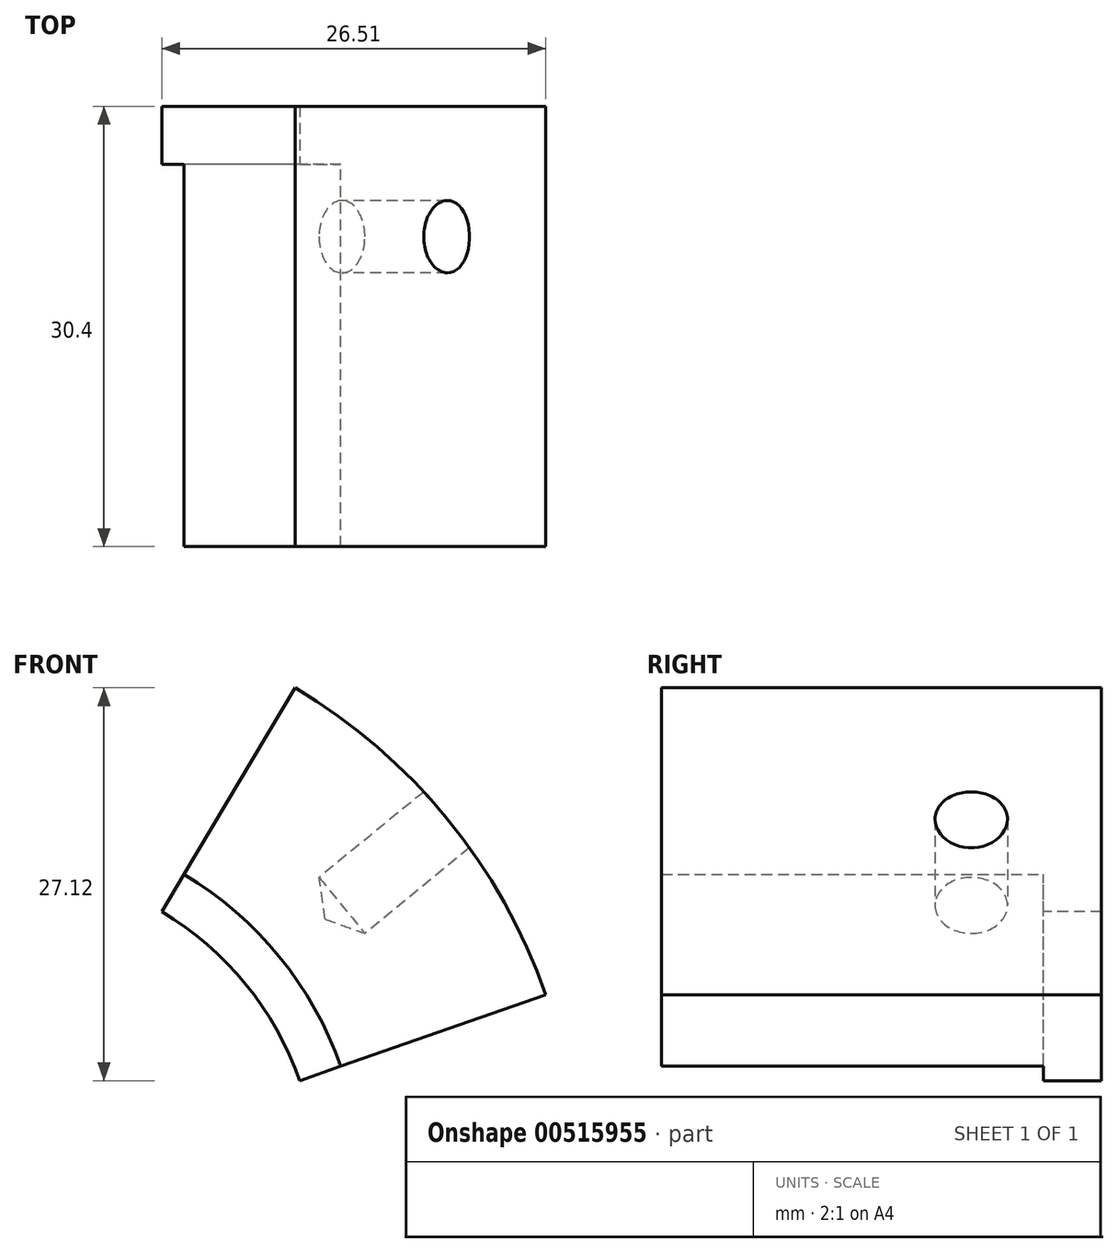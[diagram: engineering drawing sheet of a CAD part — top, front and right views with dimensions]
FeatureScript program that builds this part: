
annotation { "Feature Type Name" : "Feature", "Feature Type Description" : "" }
export const myFeature = defineFeature(function(context is Context, id is Id, definition is map)
    precondition{}
    {
        {
            var Q0;
            Q0=qCreatedBy(makeId("Front.planeOp"),FACE);
            var sketch = newSketch(context, id + "F0", { "sketchPlane" : qUnion([Q0])});
            skArc(sketch, "E0", {"start": v(37.76, 13.18) * mm, "mid": v(30.98, 25.3) * mm, "end": v(20.45, 34.37) * mm});
            skArc(sketch, "E1", {"start": v(23.6, 8.24) * mm, "mid": v(19.36, 15.82) * mm, "end": v(12.78, 21.48) * mm});
            skLineSegment(sketch, "E2", {"start": v(12.78, 21.48) * mm, "end": v(20.45, 34.37) * mm});
            skLineSegment(sketch, "E3", {"start": v(23.6, 8.24) * mm, "end": v(37.76, 13.18) * mm});
            skSolve(sketch);
        }
        {
            var Q0;
            Q0=qCreatedBy(makeId("Front.planeOp"),FACE);
            var sketch = newSketch(context, id + "F1", { "sketchPlane" : qUnion([Q0])});
            skArc(sketch, "E4", {"start": v(20.77, 7.25) * mm, "mid": v(17.04, 13.92) * mm, "end": v(11.25, 18.9) * mm});
            skLineSegment(sketch, "E5", {"start": v(20.5, 34.46) * mm, "end": v(11.25, 18.9) * mm});
            skLineSegment(sketch, "E6", {"start": v(37.76, 13.18) * mm, "end": v(20.77, 7.25) * mm});
            skArc(sketch, "E7", {"start": v(37.76, 13.18) * mm, "mid": v(30.98, 25.3) * mm, "end": v(20.45, 34.37) * mm});
            skSolve(sketch);
        }
        {
            var Q0;
            Q0=makeQuery(id+"F0.imprint","IMPRINT",FACE,{"disambiguationData":[TD([[makeQuery(id+"F0.imprint","IMPRINT",EDGE,{"derivedFrom":sQuery(id+"F0.wireOp",EDGE,"E0")}),1.0]])]});
            extrude(context, id + "F2", {"entities" : qUnion([Q0]), "depth" : 26.4 * mm, "offsetDistance" : 25 * mm});
        }
        {
            var Q0;
            Q0 = qSketchRegion(id + "F1", true);
            var Q1;
            Q1 = qSketchRegion(id + "F0", true);
            extrude(context, id + "F3", {"entities" : qUnion([Q0, Q1]), "operationType" : NewBodyOperationType.ADD, "oppositeDirection" : true, "depth" : 4 * mm, "offsetDistance" : 25 * mm});
        }
        {
            var Q0;
            Q0=makeQuery(id+"F2.opExtrude","CAP_VERTEX",VERTEX,{"disambiguationData":[OSD([sQuery(id+"F0.wireOp",EDGE,"E0"),sQuery(id+"F0.wireOp",EDGE,"E3")])],"isStart":false});
            var Q1;
            Q1=makeQuery(id+"F2.opExtrude","CAP_VERTEX",VERTEX,{"disambiguationData":[OSD([sQuery(id+"F0.wireOp",EDGE,"E0"),sQuery(id+"F0.wireOp",EDGE,"E2")])],"isStart":false});
            var Q2;
            Q2=sQuery(id+"F0.wireOp",VERTEX,"E2.end");
            cPlane(context, id + "F4", {"entities" : qUnion([Q0, Q1, Q2]), "cplaneType" : CPlaneType.THREE_POINT, "offset" : 0 * mm, "width" : 150 * mm, "height" : 150 * mm});
        }
        {
            var Q0;
            Q0=qCreatedBy(id+"F4.planeOp",FACE);
            var sketch = newSketch(context, id + "F5", { "sketchPlane" : qUnion([Q0])});
            skCircle(sketch, "E8", {"center": v(-5, 0) * mm, "radius": 2.5 * mm});
            skSolve(sketch);
        }
        {
            var Q0;
            Q0=sQuery(id+"F5.wireOp",VERTEX,"E8.center");
            var Q1;
            Q1=makeQuery(id+"F2.opExtrude","SWEPT_BODY",BODY,{"disambiguationData":[OSD([sQuery(id+"F0.wireOp",EDGE,"E0"),sQuery(id+"F0.wireOp",EDGE,"E1"),sQuery(id+"F0.wireOp",EDGE,"E2"),sQuery(id+"F0.wireOp",EDGE,"E3")])]});
            hole(context, id + "F6", {"style" : HoleStyle.SIMPLE, "endStyle" : HoleEndStyle.BLIND, "oppositeDirection" : true, "holeDiameter" : 5 * mm, "holeDepth" : 5 * mm, "isTappedThrough" : true, "tappedDepth" : 12 * mm, "tapClearance" : 3, "startFromSketch" : true, "locations" : qUnion([Q0]), "scope" : qUnion([Q1])});
        }
        {
            var Q0;
            Q0=sQuery(id+"F5.wireOp",VERTEX,"E8.center");
            var Q1;
            Q1=makeQuery(id+"F2.opExtrude","SWEPT_BODY",BODY,{"disambiguationData":[OSD([sQuery(id+"F0.wireOp",EDGE,"E0"),sQuery(id+"F0.wireOp",EDGE,"E1"),sQuery(id+"F0.wireOp",EDGE,"E2"),sQuery(id+"F0.wireOp",EDGE,"E3")])]});
            hole(context, id + "F7", {"style" : HoleStyle.SIMPLE, "endStyle" : HoleEndStyle.BLIND, "holeDiameter" : 5 * mm, "holeDepth" : 7 * mm, "isTappedThrough" : true, "tappedDepth" : 12 * mm, "tapClearance" : 3, "startFromSketch" : true, "locations" : qUnion([Q0]), "scope" : qUnion([Q1])});
        }
    });
